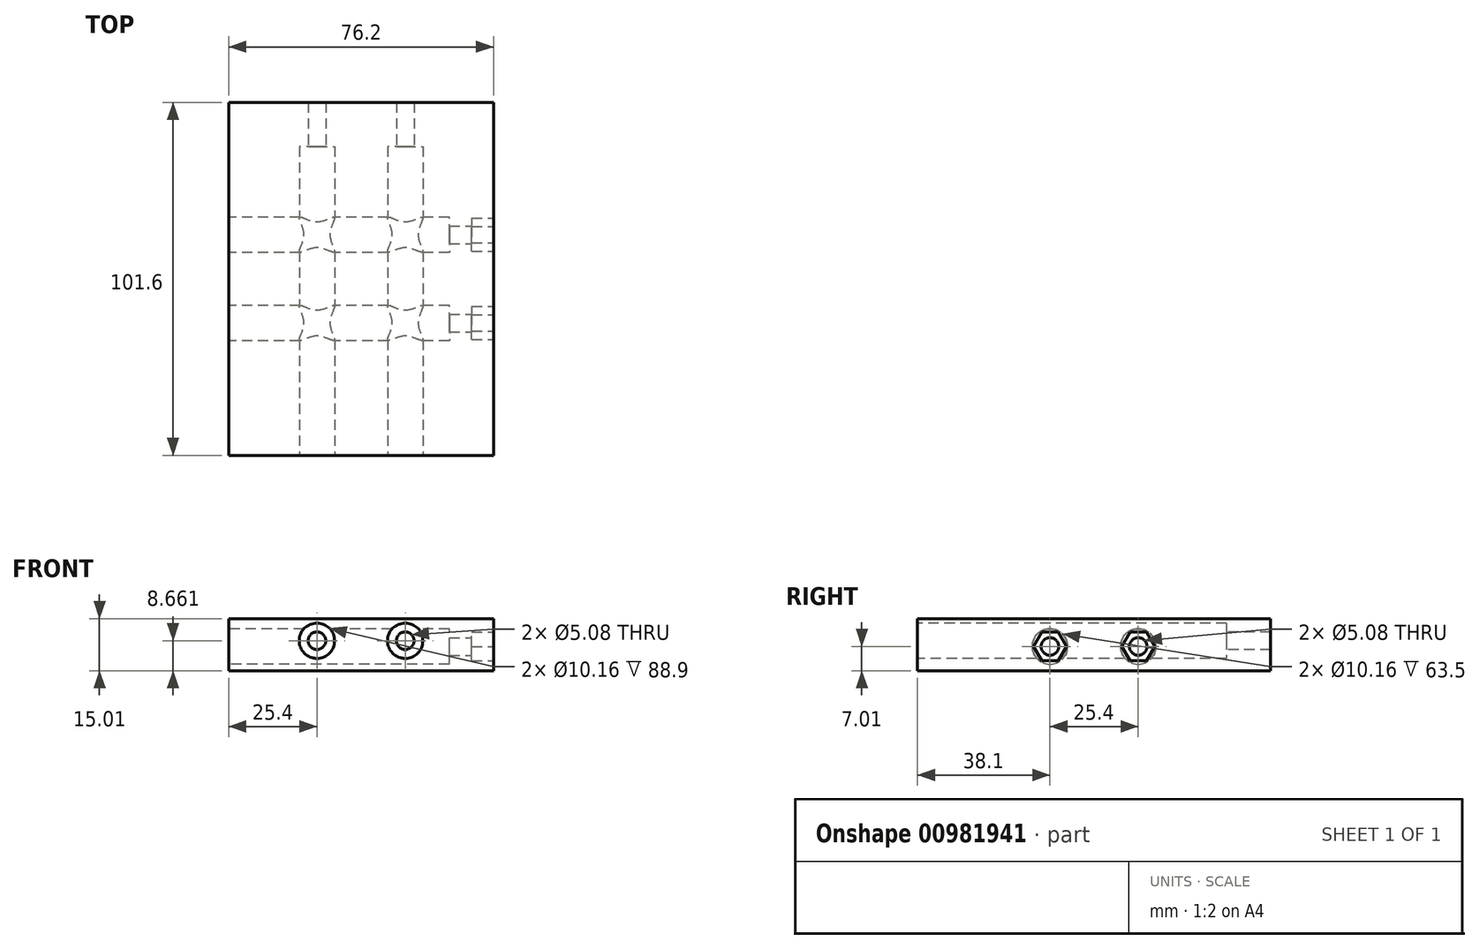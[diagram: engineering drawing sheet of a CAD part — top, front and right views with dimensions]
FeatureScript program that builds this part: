
annotation { "Feature Type Name" : "Feature", "Feature Type Description" : "" }
export const myFeature = defineFeature(function(context is Context, id is Id, definition is map)
    precondition{}
    {
        {
            var Q0;
            Q0=qCreatedBy(makeId("Top.planeOp"),FACE);
            var sketch = newSketch(context, id + "F0", { "sketchPlane" : qUnion([Q0])});
            skLineSegment(sketch, "E0.bottom", {"start": v(-38.1, 50.8) * mm, "end": v(38.1, 50.8) * mm});
            skLineSegment(sketch, "E0.top", {"start": v(-38.1, -50.8) * mm, "end": v(38.1, -50.8) * mm});
            skLineSegment(sketch, "E0.left", {"start": v(-38.1, 50.8) * mm, "end": v(-38.1, -50.8) * mm});
            skLineSegment(sketch, "E0.right", {"start": v(38.1, 50.8) * mm, "end": v(38.1, -50.8) * mm});
            skPoint(sketch, "E0.middle", {"position": v(0, 0) * mm});
            skSolve(sketch);
        }
        {
            var Q0;
            Q0=qSketchRegion(id+"F0",true);
            extrude(context, id + "F1", {"entities" : qUnion([Q0]), "depth" : 15 * mm, "offsetDistance" : 25.4 * mm});
        }
        {
            var Q0;
            Q0=makeQuery(id+"F1.opExtrude","SWEPT_FACE",FACE,{"disambiguationData":[OSD([sQuery(id+"F0.wireOp",EDGE,"E0.top")])]});
            var sketch = newSketch(context, id + "F2", { "sketchPlane" : qUnion([Q0])});
            skCircle(sketch, "E1", {"center": v(-12.7, 8.66) * mm, "radius": 2.54 * mm});
            skCircle(sketch, "E2", {"center": v(12.7, 8.66) * mm, "radius": 2.54 * mm});
            skLineSegment(sketch, "E3", {"start": v(12.7, 8.66) * mm, "end": v(-12.7, 8.66) * mm, "construction": true});
            skLineSegment(sketch, "E4", {"start": v(0, 8.66) * mm, "end": v(0, 15.01) * mm, "construction": true});
            skPoint(sketch, "E4.startSnap0", {"position": v(0, 15.01) * mm});
            skPoint(sketch, "E4.endSnap0", {"position": v(0, 15.01) * mm});
            skSolve(sketch);
        }
        {
            var Q0;
            Q0=qSketchRegion(id+"F2",true);
            extrude(context, id + "F3", {"entities" : qUnion([Q0]), "operationType" : NewBodyOperationType.REMOVE, "endBound" : BoundingType.THROUGH_ALL, "oppositeDirection" : true, "depth" : 25.4 * mm, "offsetDistance" : 25.4 * mm});
        }
        {
            var Q0;
            Q0=makeQuery(id+"F1.opExtrude","SWEPT_FACE",FACE,{"disambiguationData":[OSD([sQuery(id+"F0.wireOp",EDGE,"E0.top")])]});
            var sketch = newSketch(context, id + "F4", { "sketchPlane" : qUnion([Q0])});
            skCircle(sketch, "E5", {"center": v(-12.7, 8.66) * mm, "radius": 5.08 * mm});
            skCircle(sketch, "E6", {"center": v(12.7, 8.66) * mm, "radius": 5.08 * mm});
            skSolve(sketch);
        }
        {
            var Q0;
            Q0=qSketchRegion(id+"F4",true);
            var Q1;
            Q1=makeQuery(id+"F1.opExtrude","SWEPT_FACE",FACE,{"disambiguationData":[OSD([sQuery(id+"F0.wireOp",EDGE,"E0.bottom")])]});
            extrude(context, id + "F5", {"entities" : qUnion([Q0]), "operationType" : NewBodyOperationType.REMOVE, "endBound" : BoundingType.UP_TO_SURFACE, "oppositeDirection" : true, "depth" : 25.4 * mm, "endBoundEntityFace" : qUnion([Q1]), "hasOffset" : true, "offsetDistance" : 12.7 * mm});
        }
        {
            var Q0;
            Q0=makeQuery(id+"F1.opExtrude","SWEPT_FACE",FACE,{"disambiguationData":[OSD([sQuery(id+"F0.wireOp",EDGE,"E0.right")])]});
            var sketch = newSketch(context, id + "F6", { "sketchPlane" : qUnion([Q0])});
            skCircle(sketch, "E7.cCircle", {"center": v(-12.7, 7.01) * mm, "radius": 4.11 * mm, "construction": true});
            skLineSegment(sketch, "E7.0", {"start": v(-17.45, 7.01) * mm, "end": v(-15.07, 11.12) * mm});
            skLineSegment(sketch, "E7.1", {"start": v(-15.07, 11.12) * mm, "end": v(-10.33, 11.12) * mm});
            skLineSegment(sketch, "E7.2", {"start": v(-10.33, 11.12) * mm, "end": v(-7.95, 7.01) * mm});
            skLineSegment(sketch, "E7.3", {"start": v(-7.95, 7.01) * mm, "end": v(-10.33, 2.9) * mm});
            skLineSegment(sketch, "E7.4", {"start": v(-10.33, 2.9) * mm, "end": v(-15.07, 2.9) * mm});
            skLineSegment(sketch, "E7.5", {"start": v(-15.07, 2.9) * mm, "end": v(-17.45, 7.01) * mm});
            skPoint(sketch, "E7.0.midPoint", {"position": v(-16.26, 9.07) * mm});
            skCircle(sketch, "E8.cCircle", {"center": v(12.7, 7.01) * mm, "radius": 4.11 * mm, "construction": true});
            skLineSegment(sketch, "E8.0", {"start": v(7.95, 7.01) * mm, "end": v(10.33, 11.12) * mm});
            skLineSegment(sketch, "E8.1", {"start": v(10.33, 11.12) * mm, "end": v(15.07, 11.12) * mm});
            skLineSegment(sketch, "E8.2", {"start": v(15.07, 11.12) * mm, "end": v(17.45, 7.01) * mm});
            skLineSegment(sketch, "E8.3", {"start": v(17.45, 7.01) * mm, "end": v(15.07, 2.9) * mm});
            skLineSegment(sketch, "E8.4", {"start": v(15.07, 2.9) * mm, "end": v(10.33, 2.9) * mm});
            skLineSegment(sketch, "E8.5", {"start": v(10.33, 2.9) * mm, "end": v(7.95, 7.01) * mm});
            skPoint(sketch, "E8.0.midPoint", {"position": v(9.14, 9.07) * mm});
            skLineSegment(sketch, "E9", {"start": v(-12.7, 7.01) * mm, "end": v(-12.7, 15.01) * mm, "construction": true});
            skPoint(sketch, "E9.endSnap0", {"position": v(-12.7, 11.12) * mm});
            skLineSegment(sketch, "E10", {"start": v(-12.7, 7.01) * mm, "end": v(-12.7, 0) * mm, "construction": true});
            skSolve(sketch);
        }
        {
            var Q0;
            Q0=qSketchRegion(id+"F6",true);
            extrude(context, id + "F7", {"entities" : qUnion([Q0]), "operationType" : NewBodyOperationType.REMOVE, "oppositeDirection" : true, "depth" : 6.25 * mm, "offsetDistance" : 25.4 * mm});
        }
        {
            var Q0;
            Q0=makeQuery(id+"F7.boolean.opBoolean","COPY",FACE,{"derivedFrom":makeQuery(id+"F7.opExtrude","CAP_FACE",FACE,{"disambiguationData":[OSD([sQuery(id+"F6.wireOp",EDGE,"E7.0"),sQuery(id+"F6.wireOp",EDGE,"E7.1"),sQuery(id+"F6.wireOp",EDGE,"E7.2"),sQuery(id+"F6.wireOp",EDGE,"E7.3"),sQuery(id+"F6.wireOp",EDGE,"E7.4"),sQuery(id+"F6.wireOp",EDGE,"E7.5")])],"isStart":false})});
            var sketch = newSketch(context, id + "F8", { "sketchPlane" : qUnion([Q0])});
            skCircle(sketch, "E11", {"center": v(-12.7, 7.01) * mm, "radius": 2.54 * mm});
            skCircle(sketch, "E12", {"center": v(12.7, 7.01) * mm, "radius": 2.54 * mm});
            skSolve(sketch);
        }
        {
            var Q0;
            Q0=qSketchRegion(id+"F8",true);
            extrude(context, id + "F9", {"entities" : qUnion([Q0]), "operationType" : NewBodyOperationType.REMOVE, "endBound" : BoundingType.THROUGH_ALL, "oppositeDirection" : true, "depth" : 25.4 * mm, "offsetDistance" : 25.4 * mm});
        }
        {
            var Q0;
            Q0=makeQuery(id+"F1.opExtrude","SWEPT_FACE",FACE,{"disambiguationData":[OSD([sQuery(id+"F0.wireOp",EDGE,"E0.left")])]});
            var sketch = newSketch(context, id + "F10", { "sketchPlane" : qUnion([Q0])});
            skCircle(sketch, "E13", {"center": v(-12.7, 7.01) * mm, "radius": 5.08 * mm});
            skCircle(sketch, "E14", {"center": v(12.7, 7.01) * mm, "radius": 5.08 * mm});
            skSolve(sketch);
        }
        {
            var Q0;
            Q0=qSketchRegion(id+"F10",true);
            var Q1;
            Q1=makeQuery(id+"F1.opExtrude","SWEPT_FACE",FACE,{"disambiguationData":[OSD([sQuery(id+"F0.wireOp",EDGE,"E0.right")])]});
            extrude(context, id + "F11", {"entities" : qUnion([Q0]), "operationType" : NewBodyOperationType.REMOVE, "endBound" : BoundingType.UP_TO_SURFACE, "oppositeDirection" : true, "depth" : 25.4 * mm, "endBoundEntityFace" : qUnion([Q1]), "hasOffset" : true, "offsetDistance" : 12.7 * mm});
        }
    });
